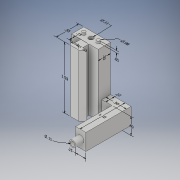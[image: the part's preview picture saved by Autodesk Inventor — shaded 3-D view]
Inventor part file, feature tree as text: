
AUTODESK INVENTOR PART (.ipt)
format: ipt  version: 2018 (Build 220112000, 112)  size: 213,504 bytes
history: native  units: in
note: dims shown in document units (in); Inventor stores cm internally (conversion verified against a paired STEP export)
features: other x15, sketch x9, extrude x7, hole x2
ambient origin geometry x8: Origin, YZ Plane, XZ Plane, XY Plane, X Axis, Y Axis, Z Axis, Center Point
bodies: Solid1 (feature_tree)
feature tree (33):
  other  "Annotations"
  extrude  "Extrusion1"  Depth=0.3in
  extrude  "Extrusion2"  Depth=0.25in
  extrude  "Extrusion3"  Depth=0.05in
  hole  "Hole1"  [1 undecoded]
  extrude  "Extrusion4"  Depth=0.1in
  sketch  "Sketch8"  dims[d10=1.5in d11=0.0in d12=0.15in]
  extrude  "Extrusion5"  Depth=0.15in
  extrude  "Extrusion6"  Depth=0.05in TaperAngle=0.0deg
  hole  "Hole2"  [1 undecoded]
  extrude  "Extrusion7"  Depth=0.2in
  sketch  "Sketch1"  dims[d0=0.65in d1=0.3in]
  sketch  "Sketch2"  dims[d2=0.1in d3=0.25in]
  sketch  "Sketch3"  dims[d4=0.2in d5=0.05in]
  sketch  "Sketch6"  dims[d6=0.1in d7=0.1in]
  sketch  "Sketch7"  dims[d8=0.1in d9=0.1in]
  sketch  "Sketch11"  dims[d14=0.08in d18=0.05in d19=0.0in]
  sketch  "Sketch12"  dims[d20=0.15in d21=0.08in]
  sketch  "Sketch13"  dims[d22=0.05in d23=0.0in d24=0.325in d25=0.11in d26=0.11in d27=0.75in d28=0.375in d29=0.25in d30=0.5635in d31=0.45in d32=0.8108in d33=0.215in d34=0.4in d35=0.5in d36=0.0in d39=0.885in d40=0.0in d41=0.125in d42=0.16in d43=0.2in d44=0.0in d45=0.11in d46=0.11in d47=0.75in d48=0.375in d49=0.25in d50=0.5635in d51=0.5in d52=0.8108in d68=0.05in d69=0.0in d53=0.2066in d54=0.0676in d55=0.4in d56=0.1242in d57=0.2866in d58=0.215in d59=0.228in d60=0.2946in d61=1.1in d62=0.1169in d63=0.3258in d64=0.25in d65=0.0498in d66=0.2036in d67=0.5in d70=1.3864in d71=0.11in d72=0.248in d73=0.3199in d74=0.3in d75=0.1337in d76=0.3315in d77=0.55in d78=0.1431in d79=0.2433in d80=0.15in d81=0.05in d82=1.5836in d83=0.08in d84=1.8694in d85=0.11in d86=0.1873in d87=0.2754in d88=1.5in d89=0.373in d90=0.3806in d91=0.2in]
  other  "Linear Dimension 1"
  other  "Linear Dimension 2"
  other  "Linear Dimension 3"
  other  "Linear Dimension 4"
  other  "Linear Dimension 5"
  other  "Diameter Dimension 1"
  other  "Linear Dimension 6"
  other  "Linear Dimension 7"
  other  "Linear Dimension 8"
  other  "Linear Dimension 9"
  other  "Diameter Dimension 2"
  other  "Diameter Dimension 3"
  other  "Linear Dimension 10"
  other  "Linear Dimension 11"
note: 2 required parameter values undecoded (feature->parameter linkage not recoverable at this tier; creation-order binding heuristic only, values carry confidence <= 0.55)
